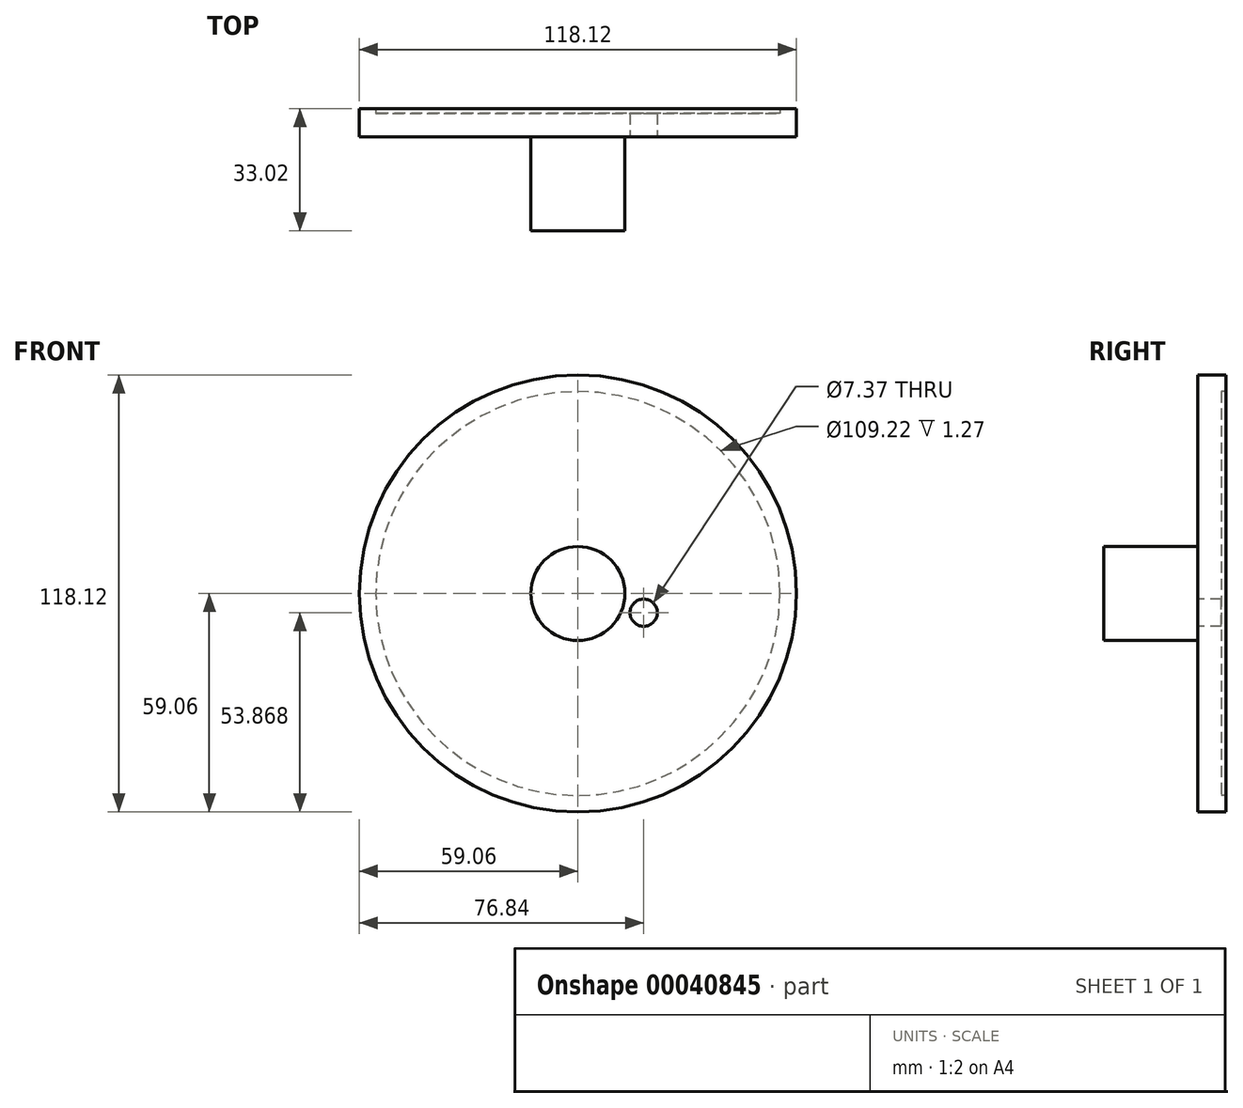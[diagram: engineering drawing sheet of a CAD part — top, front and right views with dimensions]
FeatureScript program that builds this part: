
annotation { "Feature Type Name" : "Feature", "Feature Type Description" : "" }
export const myFeature = defineFeature(function(context is Context, id is Id, definition is map)
    precondition{}
    {
        {
            var Q0;
            Q0=qCreatedBy(makeId("Front.planeOp"),FACE);
            var sketch = newSketch(context, id + "F0", { "sketchPlane" : qUnion([Q0])});
            skCircle(sketch, "E0", {"center": v(0, 0) * mm, "radius": 59.06 * mm});
            skSolve(sketch);
        }
        {
            var Q0;
            Q0=qCreatedBy(makeId("Front.planeOp"),FACE);
            var sketch = newSketch(context, id + "F1", { "sketchPlane" : qUnion([Q0])});
            skCircle(sketch, "E1", {"center": v(0, 0) * mm, "radius": 12.7 * mm});
            skSolve(sketch);
        }
        {
            var Q0;
            Q0 = qSketchRegion(id + "F1", true);
            extrude(context, id + "F2", {"entities" : qUnion([Q0]), "depth" : 25.4 * mm});
        }
        {
            var Q0;
            Q0 = qSketchRegion(id + "F0", true);
            extrude(context, id + "F3", {"entities" : qUnion([Q0]), "operationType" : NewBodyOperationType.ADD, "oppositeDirection" : true, "depth" : 6.35 * mm});
        }
        {
            var Q0;
            Q0=qCreatedBy(makeId("Front.planeOp"),FACE);
            var sketch = newSketch(context, id + "F4", { "sketchPlane" : qUnion([Q0])});
            skCircle(sketch, "E2", {"center": v(17.78, -5.2) * mm, "radius": 3.68 * mm});
            skSolve(sketch);
        }
        {
            var Q0;
            Q0 = qSketchRegion(id + "F4", true);
            extrude(context, id + "F5", {"entities" : qUnion([Q0]), "operationType" : NewBodyOperationType.REMOVE, "endBound" : BoundingType.THROUGH_ALL, "oppositeDirection" : true, "depth" : 25.4 * mm});
        }
        {
            var Q0;
            Q0=makeQuery(id+"F3.opExtrude","CAP_FACE",FACE,{"disambiguationData":[OSD([sQuery(id+"F0.wireOp",EDGE,"E0")])],"isStart":false});
            var sketch = newSketch(context, id + "F6", { "sketchPlane" : qUnion([Q0])});
            skCircle(sketch, "E3", {"center": v(0, 0) * mm, "radius": 54.61 * mm});
            skCircle(sketch, "E4.0", {"center": v(0, 0) * mm, "radius": 59.06 * mm});
            skSolve(sketch);
        }
        {
            var Q0;
            Q0=makeQuery(id+"F6.imprint","IMPRINT",FACE,{"disambiguationData":[TD([[makeQuery(id+"F6.imprint","IMPRINT",EDGE,{"derivedFrom":sQuery(id+"F6.wireOp",EDGE,"E3")}),-1.0]])]});
            extrude(context, id + "F7", {"entities" : qUnion([Q0]), "operationType" : NewBodyOperationType.ADD, "depth" : 1.27 * mm});
        }
    });
